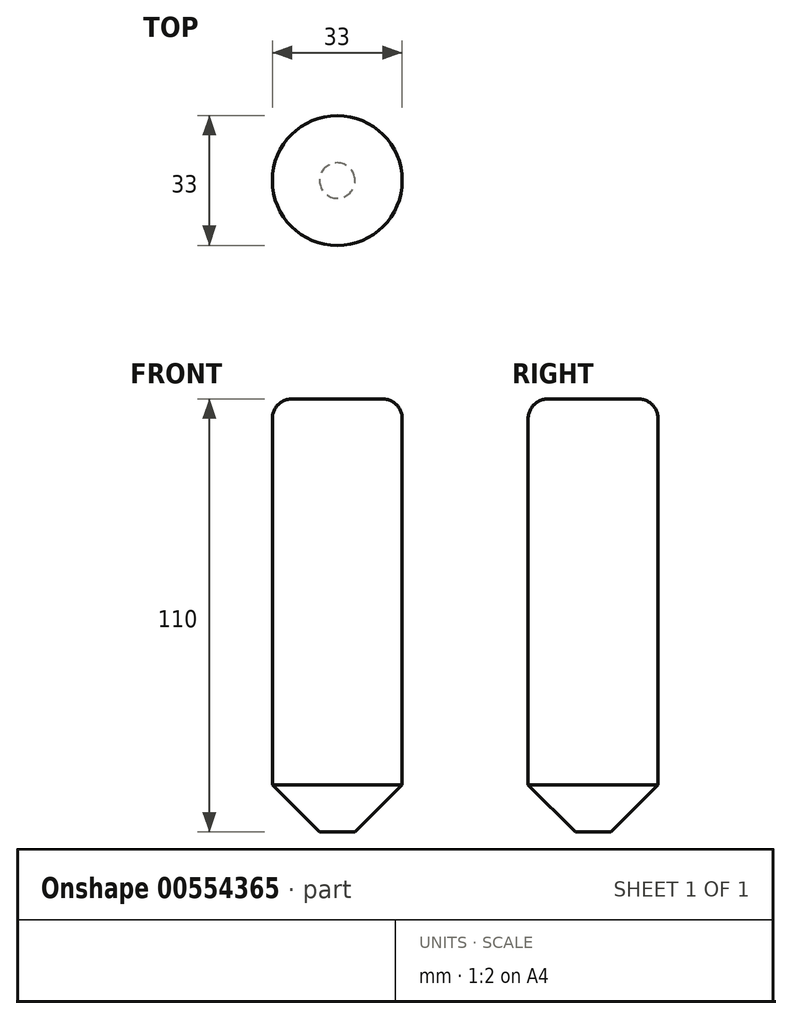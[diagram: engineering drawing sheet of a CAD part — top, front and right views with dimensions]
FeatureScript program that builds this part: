
annotation { "Feature Type Name" : "Feature", "Feature Type Description" : "" }
export const myFeature = defineFeature(function(context is Context, id is Id, definition is map)
    precondition{}
    {
        {
            var Q0;
            Q0=qCreatedBy(makeId("Top.planeOp"),FACE);
            var sketch = newSketch(context, id + "F0", { "sketchPlane" : qUnion([Q0])});
            skCircle(sketch, "E0", {"center": v(0, 0) * mm, "radius": 16.5 * mm});
            skSolve(sketch);
        }
        {
            var Q0;
            Q0 = qSketchRegion(id + "F0", true);
            extrude(context, id + "F1", {"entities" : qUnion([Q0]), "depth" : 110 * mm, "offsetDistance" : 25 * mm});
        }
        {
            var Q0;
            Q0=makeQuery(id+"F1.opExtrude","CAP_EDGE",EDGE,{"disambiguationData":[OSD([sQuery(id+"F0.wireOp",EDGE,"E0")])],"isStart":true});
            chamfer(context, id + "F2", {"entities" : qUnion([Q0]), "width" : 12 * mm, "tangentPropagation" : true});
        }
        {
            var Q0;
            Q0=makeQuery(id+"F1.opExtrude","CAP_EDGE",EDGE,{"disambiguationData":[OSD([sQuery(id+"F0.wireOp",EDGE,"E0")])],"isStart":false});
            fillet(context, id + "F3", {"entities" : qUnion([Q0]), "radius" : 5 * mm, "tangentPropagation" : true, "allowEdgeOverflow" : false});
        }
    });
